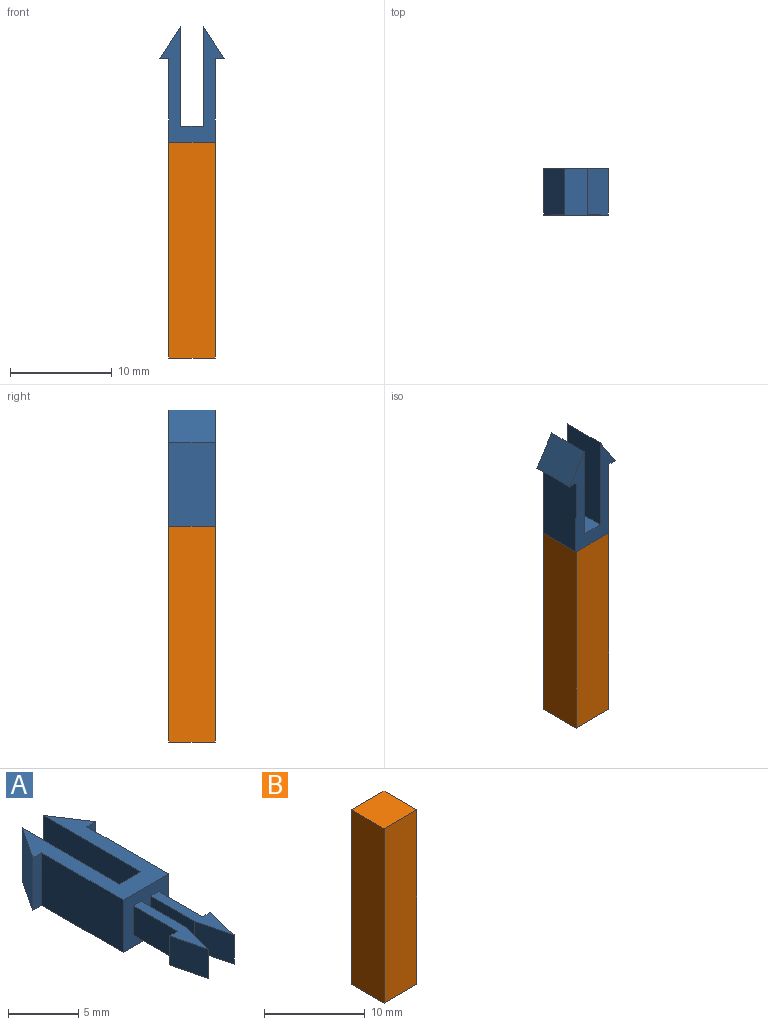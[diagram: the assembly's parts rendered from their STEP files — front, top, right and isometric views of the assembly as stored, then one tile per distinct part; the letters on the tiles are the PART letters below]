
ASSEMBLY  parts=2 mates=1
PART A: 26 faces, bbox 6.4x19.1x4.6 mm
  f0: plane 4.45x2.54mm, normal (-1,0,0), area 11.3mm2, adj f1,f13,f24,f25
  f1: plane 2.54x0.8mm, normal (0,1,0), area 2mm2, adj f0,f2,f24,f25
  f2: plane 3.18x2.54mm, normal (-0.97,-0.24,0), area 8.3mm2, adj f1,f3,f24,f25
  f3: plane 3.18x2.54mm, normal (0.97,-0.24,0), area 8.3mm2, adj f2,f4,f24,f25
  f4: plane 4.45x2.54mm, normal (1,0,0), area 11.3mm2, adj f3,f13,f24,f25
  f5: plane 4.45x2.54mm, normal (-1,0,0), area 11.3mm2, adj f6,f13,f22,f23
  f6: plane 3.18x2.54mm, normal (-0.97,-0.24,0), area 8.3mm2, adj f5,f7,f22,f23
  f7: plane 3.18x2.54mm, normal (0.97,-0.24,0), area 8.3mm2, adj f6,f8,f22,f23
  f8: plane 2.54x0.8mm, normal (0,1,0), area 2mm2, adj f7,f9,f22,f23
  f9: plane 4.45x2.54mm, normal (1,0,0), area 11.3mm2, adj f8,f13,f22,f23
  f10: plane 11.43x6.35mm, normal (0,0,1), area 29.9mm2, adj f12,f13,f14,f15,f16,f17,f18,f19
  f11: plane 11.43x6.35mm, normal (0,0,-1), area 29.9mm2, adj f12,f13,f14,f15,f16,f17,f18,f19
  f12: plane 8.26x4.57mm, normal (-1,0,0), area 37.7mm2, adj f10,f11,f13,f21
  f13: plane 4.57x4.57mm, normal (0,-1,0), area 16.8mm2, adj f0,f4,f5,f9,f10,f11,f12,f14
  f14: plane 8.26x4.57mm, normal (1,0,0), area 37.7mm2, adj f10,f11,f13,f15
  f15: plane 4.57x0.89mm, normal (0,-1,0), area 4.1mm2, adj f10,f11,f14,f16
  f16: plane 4.57x3.18mm, normal (0.84,0.55,0), area 17.4mm2, adj f10,f11,f15,f17
  f17: plane 9.84x4.57mm, normal (-1,0,0), area 45mm2, adj f10,f11,f16,f18
  f18: plane 4.57x2.17mm, normal (0,1,0), area 9.9mm2, adj f10,f11,f17,f19
  f19: plane 9.84x4.57mm, normal (1,0,0), area 45mm2, adj f10,f11,f18,f20
  f20: plane 4.57x3.18mm, normal (-0.84,0.55,0), area 17.4mm2, adj f10,f11,f19,f21
  f21: plane 4.57x0.89mm, normal (0,-1,0), area 4.1mm2, adj f10,f11,f12,f20
  f22: plane 7.62x1.6mm, normal (0,0,-1), area 6.1mm2, adj f5,f6,f7,f8,f9,f13
  f23: plane 7.62x1.6mm, normal (0,0,1), area 6.1mm2, adj f5,f6,f7,f8,f9,f13
  f24: plane 7.62x1.6mm, normal (0,0,-1), area 6.1mm2, adj f0,f1,f2,f3,f4,f13
  f25: plane 7.62x1.6mm, normal (0,0,1), area 6.1mm2, adj f0,f1,f2,f3,f4,f13
PART B: 6 faces, bbox 4.6x4.6x21.2 mm
  f0: plane 21.21x4.57mm, normal (1,0,0), area 97mm2, adj f1,f3,f4,f5
  f1: plane 21.21x4.57mm, normal (0,1,0), area 97mm2, adj f0,f2,f4,f5
  f2: plane 21.21x4.57mm, normal (-1,0,0), area 97mm2, adj f1,f3,f4,f5
  f3: plane 21.21x4.57mm, normal (0,-1,0), area 97mm2, adj f0,f2,f4,f5
  f4: plane 4.57x4.57mm, normal (0,0,1), area 20.9mm2, adj f0,f1,f2,f3
  f5: plane 4.57x4.57mm, normal (0,0,-1), area 20.9mm2, adj f0,f1,f2,f3
PLACE A rot(axis=(1,0,0),90deg) t=(-5.95,2.7,0.58)mm
PLACE B t=(-5.95,2.7,-21.42)mm
MATE planar A.f13 <-> B.f4  axis (0,0,-1) through (-5.95,2.7,-0.21)mm
